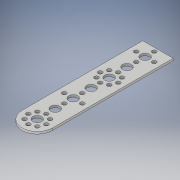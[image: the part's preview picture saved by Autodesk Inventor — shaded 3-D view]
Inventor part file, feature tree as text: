
AUTODESK INVENTOR PART (.ipt)
format: ipt  version: 2019 (Build 230136000, 136)  size: 192,512 bytes
history: native  units: in
note: dims shown in document units (in); Inventor stores cm internally (conversion verified against a paired STEP export)
features: extrude x2, sketch x2
ambient origin geometry x8: Origin, YZ Plane, XZ Plane, XY Plane, X Axis, Y Axis, Z Axis, Center Point
bodies: Solid1 (feature_tree)
feature tree (4):
  extrude  "Extrusion1"  Depth=0.0787in TaperAngle=0.0deg
  extrude  "Extrusion2"  [1 undecoded]
  sketch  "Sketch1"  dims[d0=0.0787in d1=0.0in d2=1.0in d3=0.0in]
  sketch  "Sketch2"
note: 1 required parameter value undecoded (feature->parameter linkage not recoverable at this tier; creation-order binding heuristic only, values carry confidence <= 0.55)
